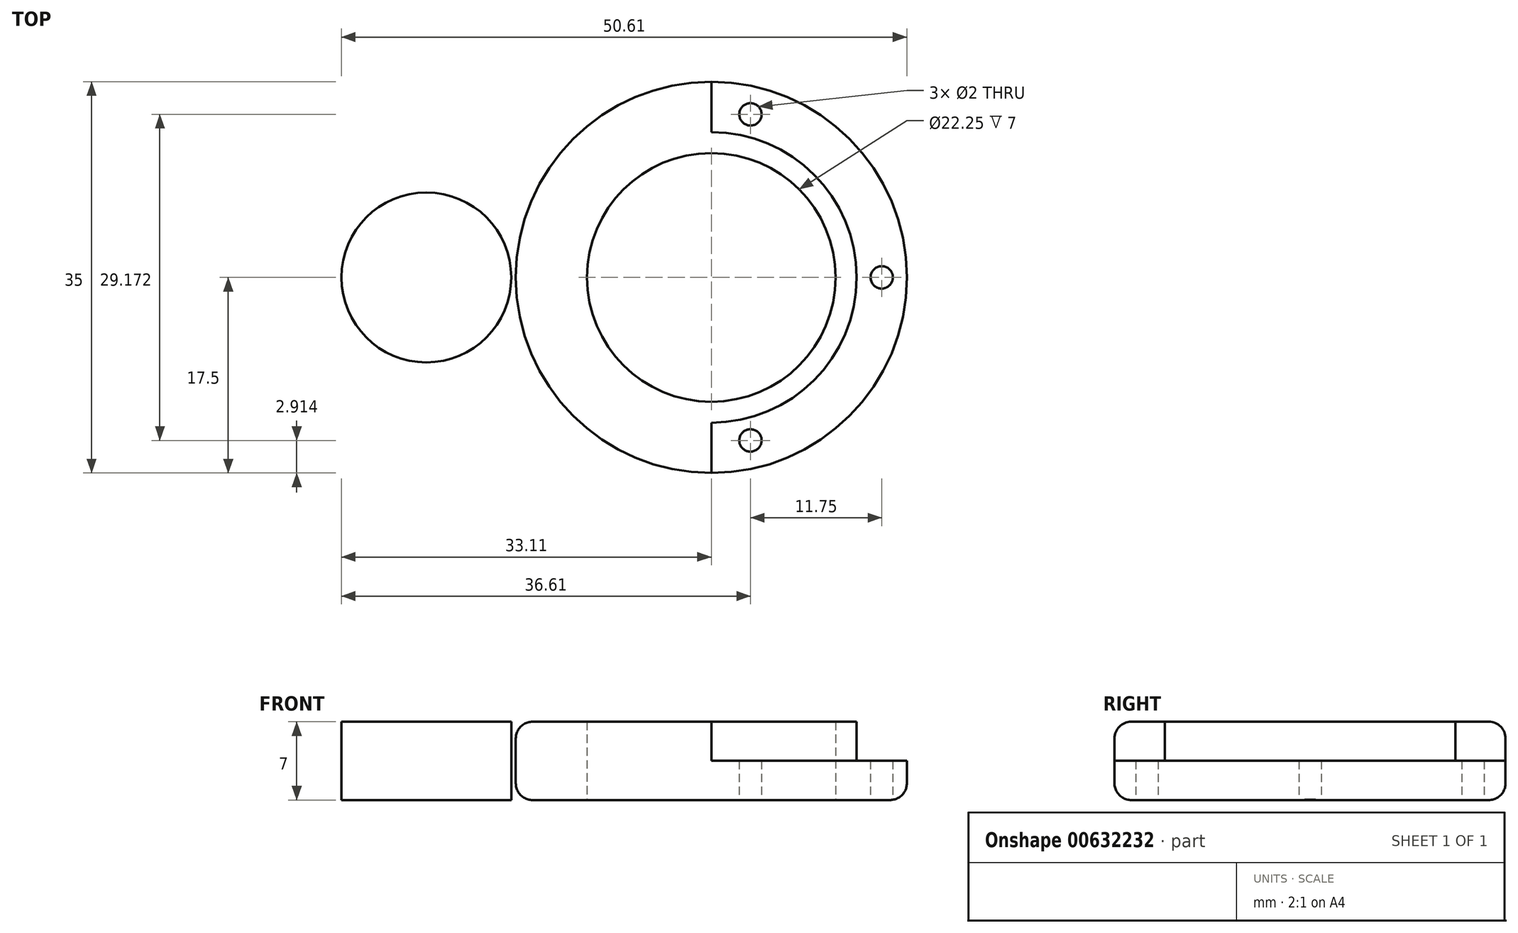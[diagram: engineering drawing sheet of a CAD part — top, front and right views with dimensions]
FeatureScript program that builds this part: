
annotation { "Feature Type Name" : "Feature", "Feature Type Description" : "" }
export const myFeature = defineFeature(function(context is Context, id is Id, definition is map)
    precondition{}
    {
        {
            var Q0;
            Q0=qCreatedBy(makeId("Top.planeOp"),FACE);
            var sketch = newSketch(context, id + "F0", { "sketchPlane" : qUnion([Q0])});
            skCircle(sketch, "E0", {"center": v(0, 0) * mm, "radius": 11.12 * mm});
            skCircle(sketch, "E1", {"center": v(0, 0) * mm, "radius": 17.5 * mm});
            skLineSegment(sketch, "E2", {"start": v(0, 0) * mm, "end": v(34.83, 0) * mm, "construction": true});
            skCircle(sketch, "E3", {"center": v(25.5, 0) * mm, "radius": 7.6 * mm});
            skArc(sketch, "E4", {"start": v(21.65, -11.36) * mm, "mid": v(37.5, 0) * mm, "end": v(21.65, 11.36) * mm});
            skArc(sketch, "E5", {"start": v(23.21, -11.78) * mm, "mid": v(17.5, -11.12) * mm, "end": v(11.98, -12.75) * mm});
            skArc(sketch, "E6.MirrorCS", {"start": v(23.21, 11.78) * mm, "mid": v(17.5, 11.12) * mm, "end": v(11.98, 12.75) * mm});
            skLineSegment(sketch, "E7.MirrorCS", {"start": v(0, 0) * mm, "end": v(-34.83, 0) * mm, "construction": true});
            skCircle(sketch, "E8.MirrorC", {"center": v(-25.5, 0) * mm, "radius": 7.6 * mm});
            skArc(sketch, "E9.MirrorC", {"start": v(-21.65, -11.36) * mm, "mid": v(-37.5, 0) * mm, "end": v(-21.65, 11.36) * mm});
            skArc(sketch, "E10.MirrorCS", {"start": v(-23.21, -11.78) * mm, "mid": v(-17.5, -11.12) * mm, "end": v(-11.98, -12.75) * mm});
            skArc(sketch, "E11.MirrorCS", {"start": v(-23.21, 11.78) * mm, "mid": v(-17.5, 11.12) * mm, "end": v(-11.98, 12.75) * mm});
            skCircle(sketch, "E12", {"center": v(3.5, 14.59) * mm, "radius": 0.75 * mm});
            skPoint(sketch, "E13.endSnap0", {"position": v(0, -14.75) * mm});
            skCircle(sketch, "E14", {"center": v(0, 0) * mm, "radius": 13 * mm});
            skCircle(sketch, "E15", {"center": v(3.5, 14.59) * mm, "radius": 1 * mm});
            skCircle(sketch, "E16.MirrorC", {"center": v(3.5, -14.59) * mm, "radius": 1 * mm});
            skCircle(sketch, "E17.MirrorC", {"center": v(3.5, -14.59) * mm, "radius": 0.75 * mm});
            skLineSegment(sketch, "E18", {"start": v(0, 13) * mm, "end": v(0, 17.5) * mm});
            skLineSegment(sketch, "E19", {"start": v(0, -17.5) * mm, "end": v(0, -13) * mm});
            skCircle(sketch, "E20.MirrorC", {"center": v(15.25, 0) * mm, "radius": 1 * mm});
            skCircle(sketch, "E21.MirrorC", {"center": v(15.25, 0) * mm, "radius": 0.75 * mm});
            skLineSegment(sketch, "E22", {"start": v(13, 0) * mm, "end": v(17.5, 0) * mm, "construction": true});
            skSolve(sketch);
        }
        {
            var Q0;
            {var subQ0=sQuery(id+"F0.wireOp",EDGE,"E18");Q0=makeQuery(id+"F0.imprint","IMPRINT",FACE,{"disambiguationData":[TD([[makeQuery(id+"F0.imprint","IMPRINT",EDGE,{"derivedFrom":subQ0}),1.0]])]});}
            var Q1;
            Q1=makeQuery(id+"F0.imprint","IMPRINT",FACE,{"disambiguationData":[TD([[makeQuery(id+"F0.imprint","IMPRINT",EDGE,{"derivedFrom":sQuery(id+"F0.wireOp",EDGE,"E8.MirrorC")}),1.0]])]});
            var Q2;
            Q2=makeQuery(id+"F0.imprint","IMPRINT",FACE,{"disambiguationData":[TD([[makeQuery(id+"F0.imprint","IMPRINT",EDGE,{"derivedFrom":sQuery(id+"F0.wireOp",EDGE,"E0")}),-1.0]])]});
            extrude(context, id + "F1", {"entities" : qUnion([Q0, Q1, Q2]), "depth" : 7 * mm, "offsetDistance" : 25 * mm});
        }
        {
            var Q0;
            Q0=makeQuery(id+"F0.imprint","IMPRINT",FACE,{"disambiguationData":[TD([[makeQuery(id+"F0.imprint","IMPRINT",EDGE,{"derivedFrom":sQuery(id+"F0.wireOp",EDGE,"E15")}),-1.0]])]});
            extrude(context, id + "F2", {"entities" : qUnion([Q0]), "operationType" : NewBodyOperationType.ADD, "depth" : 3.5 * mm, "offsetDistance" : 25 * mm});
        }
        {
            var Q0;
            {var subQ0=sQuery(id+"F0.wireOp",EDGE,"E1");Q0=makeQuery(id+"F1.opExtrude","CAP_EDGE",EDGE,{"disambiguationData":[OSD([subQ0]),TDD([makeQuery(id+"F0.imprint","IMPRINT",EDGE,{"disambiguationData":[TD([[makeQuery(id+"F0.imprint","INTERSECT",VERTEX,{"derivedFrom":[subQ0,sQuery(id+"F0.wireOp",EDGE,"E10.MirrorCS")]}),-1.0]])],"derivedFrom":subQ0})])],"isStart":false});}
            var Q1;
            Q1=makeQuery(id+"F1.opExtrude","CAP_EDGE",EDGE,{"disambiguationData":[OSD([sQuery(id+"F0.wireOp",EDGE,"E10.MirrorCS")])],"isStart":false});
            var Q2;
            Q2=makeQuery(id+"F1.opExtrude","CAP_EDGE",EDGE,{"disambiguationData":[OSD([sQuery(id+"F0.wireOp",EDGE,"E9.MirrorC")])],"isStart":false});
            var Q3;
            Q3=makeQuery(id+"F1.opExtrude","CAP_EDGE",EDGE,{"disambiguationData":[OSD([sQuery(id+"F0.wireOp",EDGE,"E11.MirrorCS")])],"isStart":false});
            var Q4;
            {var subQ0=sQuery(id+"F0.wireOp",EDGE,"E1");Q4=makeQuery(id+"F1.opExtrude","CAP_EDGE",EDGE,{"disambiguationData":[OSD([subQ0]),TDD([makeQuery(id+"F0.imprint","IMPRINT",EDGE,{"disambiguationData":[TD([[makeQuery(id+"F0.imprint","INTERSECT",VERTEX,{"derivedFrom":[subQ0,sQuery(id+"F0.wireOp",EDGE,"E11.MirrorCS")]}),1.0]])],"derivedFrom":subQ0})])],"isStart":false});}
            var Q5;
            Q5=makeQuery(id+"F1.opExtrude","CAP_EDGE",EDGE,{"disambiguationData":[OSD([sQuery(id+"F0.wireOp",EDGE,"E11.MirrorCS")])],"isStart":true});
            var Q6;
            Q6=makeQuery(id+"F1.opExtrude","CAP_EDGE",EDGE,{"disambiguationData":[OSD([sQuery(id+"F0.wireOp",EDGE,"E9.MirrorC")])],"isStart":true});
            var Q7;
            Q7=makeQuery(id+"F1.opExtrude","CAP_EDGE",EDGE,{"disambiguationData":[OSD([sQuery(id+"F0.wireOp",EDGE,"E10.MirrorCS")])],"isStart":true});
            var Q8;
            {var subQ0=sQuery(id+"F0.wireOp",EDGE,"E1");Q8=makeQuery(id+"F2.boolean.opBoolean","MERGE",EDGE,{"derivedFrom":[makeQuery(id+"F1.opExtrude","CAP_EDGE",EDGE,{"disambiguationData":[OSD([subQ0]),TDD([makeQuery(id+"F0.imprint","IMPRINT",EDGE,{"disambiguationData":[TD([[makeQuery(id+"F0.imprint","INTERSECT",VERTEX,{"derivedFrom":[subQ0,sQuery(id+"F0.wireOp",EDGE,"E11.MirrorCS")]}),1.0]])],"derivedFrom":subQ0})])],"isStart":true}),makeQuery(id+"F1.opExtrude","CAP_EDGE",EDGE,{"disambiguationData":[OSD([subQ0]),TDD([makeQuery(id+"F0.imprint","IMPRINT",EDGE,{"disambiguationData":[TD([[makeQuery(id+"F0.imprint","INTERSECT",VERTEX,{"derivedFrom":[subQ0,sQuery(id+"F0.wireOp",EDGE,"E10.MirrorCS")]}),-1.0]])],"derivedFrom":subQ0})])],"isStart":true}),makeQuery(id+"F2.opExtrude","CAP_EDGE",EDGE,{"disambiguationData":[OSD([subQ0])],"isStart":true})]});}
            fillet(context, id + "F3", {"entities" : qUnion([Q0, Q1, Q2, Q3, Q4, Q5, Q6, Q7, Q8]), "radius" : 1.5 * mm, "tangentPropagation" : true, "allowEdgeOverflow" : false});
        }
    });
